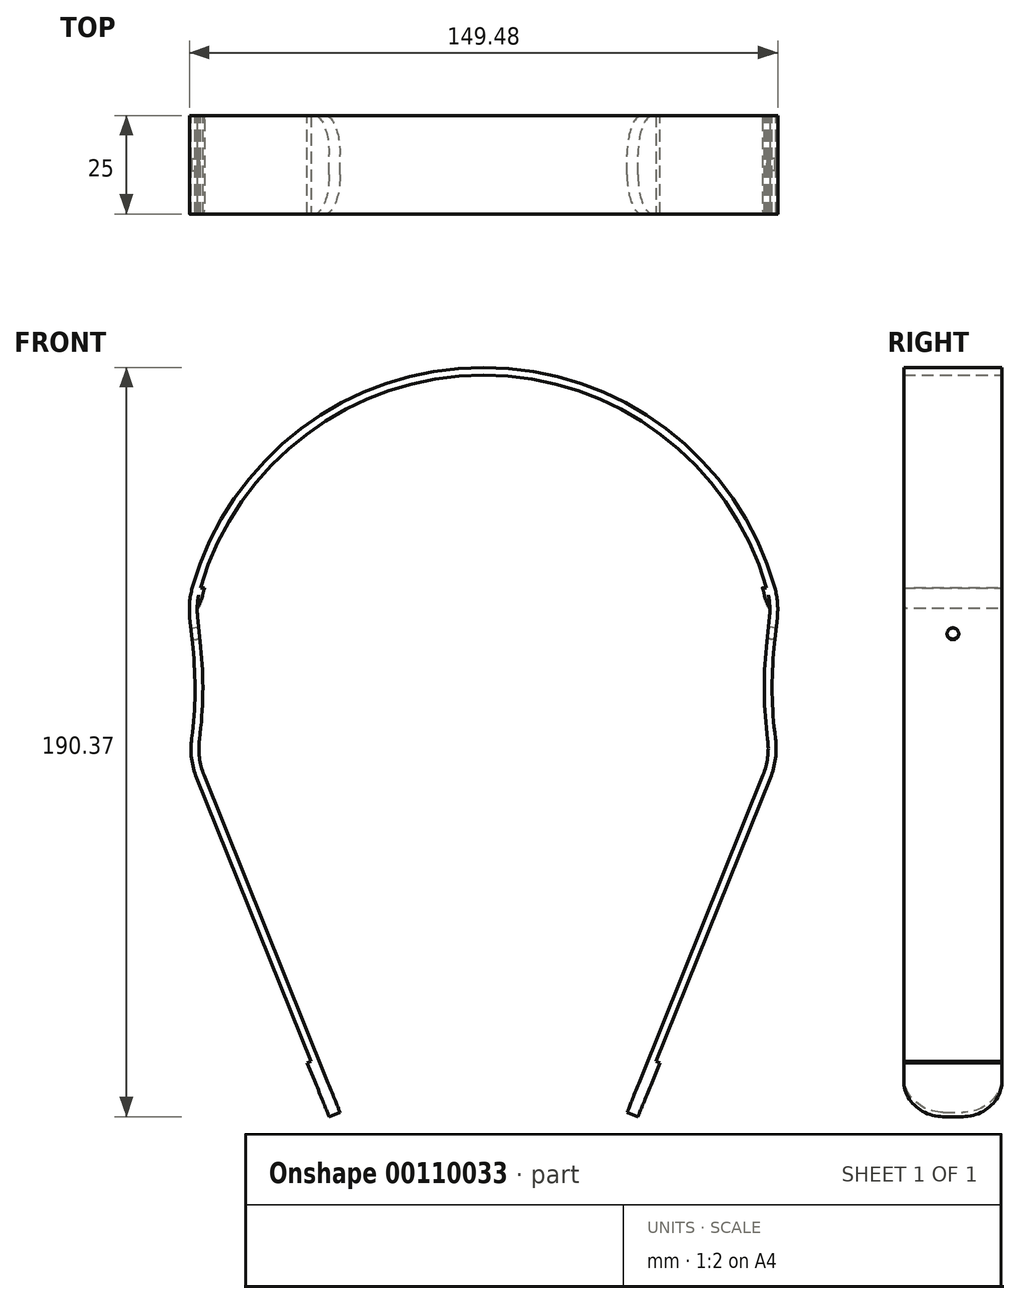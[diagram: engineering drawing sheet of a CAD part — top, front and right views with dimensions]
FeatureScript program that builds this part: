
annotation { "Feature Type Name" : "Feature", "Feature Type Description" : "" }
export const myFeature = defineFeature(function(context is Context, id is Id, definition is map)
    precondition{}
    {
        {
            var Q0;
            Q0=qCreatedBy(makeId("Front.planeOp"),FACE);
            var sketch = newSketch(context, id + "F0", { "sketchPlane" : qUnion([Q0])});
            skLineSegment(sketch, "E0", {"start": v(0, 0) * mm, "end": v(0, 60) * mm, "construction": true});
            skLineSegment(sketch, "E1", {"start": v(0, 0) * mm, "end": v(-75, 0) * mm, "construction": true});
            skArc(sketch, "E2", {"start": v(0, 60) * mm, "mid": v(-46.4, 44.41) * mm, "end": v(-74, 3.98) * mm});
            skLineSegment(sketch, "E3", {"start": v(-74.64, -3.51) * mm, "end": v(-73.83, -11.25) * mm});
            skPoint(sketch, "E4.visualSharp", {"position": v(-75, 0) * mm});
            skArc(sketch, "E4.filletArc", {"start": v(-74, 3.98) * mm, "mid": v(-74.67, 0.26) * mm, "end": v(-74.64, -3.51) * mm});
            skPoint(sketch, "E5.visualSharp", {"position": v(-73.28, -16.58) * mm});
            skArc(sketch, "E5.filletArc", {"start": v(-74.15, -34.24) * mm, "mid": v(-73.32, -22.75) * mm, "end": v(-73.83, -11.25) * mm});
            skPoint(sketch, "E6.visualSharp", {"position": v(-83.24, -38.88) * mm});
            skPoint(sketch, "E7.orphan", {"position": v(75, 0) * mm});
            skLineSegment(sketch, "E8", {"start": v(-38.32, -130) * mm, "end": v(-72.87, -44.34) * mm});
            skPoint(sketch, "E9.visualSharp", {"position": v(-74.94, -39.21) * mm});
            skArc(sketch, "E9.filletArc", {"start": v(-74.15, -34.24) * mm, "mid": v(-74.17, -39.37) * mm, "end": v(-72.87, -44.34) * mm});
            skLineSegment(sketch, "E10.0", {"start": v(-36.47, -129.25) * mm, "end": v(-71.02, -43.6) * mm});
            skArc(sketch, "E10.1", {"start": v(-72.17, -34.5) * mm, "mid": v(-72.18, -39.12) * mm, "end": v(-71.02, -43.6) * mm});
            skArc(sketch, "E10.2", {"start": v(0, 58) * mm, "mid": v(-45.2, 42.82) * mm, "end": v(-72.07, 3.44) * mm});
            skArc(sketch, "E10.3", {"start": v(-72.07, 3.44) * mm, "mid": v(-72.68, 0.1) * mm, "end": v(-72.65, -3.3) * mm});
            skLineSegment(sketch, "E10.4", {"start": v(-72.65, -3.3) * mm, "end": v(-71.84, -11.04) * mm});
            skArc(sketch, "E10.5", {"start": v(-72.17, -34.5) * mm, "mid": v(-71.32, -22.78) * mm, "end": v(-71.84, -11.04) * mm});
            skLineSegment(sketch, "E11", {"start": v(0, 58) * mm, "end": v(0, 60) * mm});
            skLineSegment(sketch, "E12", {"start": v(-38.32, -130) * mm, "end": v(-36.47, -129.25) * mm});
            skSolve(sketch);
        }
        {
            var Q0;
            Q0=makeQuery(id+"F0.imprint","IMPRINT",FACE,{"disambiguationData":[TD([[makeQuery(id+"F0.imprint","IMPRINT",EDGE,{"derivedFrom":sQuery(id+"F0.wireOp",EDGE,"E2")}),1.0]])]});
            extrude(context, id + "F1", {"entities" : qUnion([Q0]), "depth" : 25 * mm});
        }
        {
            var Q0;
            Q0=makeQuery(id+"F1.opExtrude","CAP_EDGE",EDGE,{"disambiguationData":[OSD([sQuery(id+"F0.wireOp",EDGE,"E12")])],"isStart":false});
            var Q1;
            Q1=makeQuery(id+"F1.opExtrude","CAP_EDGE",EDGE,{"disambiguationData":[OSD([sQuery(id+"F0.wireOp",EDGE,"E12")])],"isStart":true});
            fillet(context, id + "F2", {"entities" : qUnion([Q0, Q1]), "radius" : 10 * mm, "tangentPropagation" : true, "allowEdgeOverflow" : false});
        }
        {
            var Q0;
            Q0=makeQuery(id+"F1.opExtrude","SWEPT_FACE",FACE,{"disambiguationData":[OSD([sQuery(id+"F0.wireOp",EDGE,"E10.4")])]});
            var sketch = newSketch(context, id + "F3", { "sketchPlane" : qUnion([Q0])});
            skCircle(sketch, "E13", {"center": v(-12.5, 0) * mm, "radius": 1.5 * mm});
            skSolve(sketch);
        }
        {
            var Q0;
            Q0=makeQuery(id+"F3.imprint","IMPRINT",FACE,{"disambiguationData":[TD([[makeQuery(id+"F3.imprint","IMPRINT",EDGE,{"derivedFrom":sQuery(id+"F3.wireOp",EDGE,"E13")}),1.0]])]});
            extrude(context, id + "F4", {"entities" : qUnion([Q0]), "operationType" : NewBodyOperationType.REMOVE, "oppositeDirection" : true, "depth" : 25 * mm});
        }
        {
            var Q0;
            Q0=makeQuery(id+"F1.opExtrude","SWEPT_FACE",FACE,{"disambiguationData":[OSD([sQuery(id+"F0.wireOp",EDGE,"E10.0")])]});
            var sketch = newSketch(context, id + "F5", { "sketchPlane" : qUnion([Q0])});
            skLineSegment(sketch, "E14", {"start": v(-25, -91.47) * mm, "end": v(0, -91.47) * mm});
            skLineSegment(sketch, "E15.0", {"start": v(-15, -106.23) * mm, "end": v(-10, -106.23) * mm});
            skArc(sketch, "E15.1", {"start": v(-10, -106.23) * mm, "mid": v(-2.93, -103.3) * mm, "end": v(0, -96.23) * mm});
            skArc(sketch, "E15.2", {"start": v(-25, -96.23) * mm, "mid": v(-22.07, -103.3) * mm, "end": v(-15, -106.23) * mm});
            skLineSegment(sketch, "E15.3", {"start": v(-25, -96.23) * mm, "end": v(-25, -91.47) * mm});
            skLineSegment(sketch, "E15.4", {"start": v(0, -96.23) * mm, "end": v(0, -91.47) * mm});
            skSolve(sketch);
        }
        {
            var Q0;
            Q0 = qSketchRegion(id + "F5", true);
            extrude(context, id + "F6", {"entities" : qUnion([Q0]), "operationType" : NewBodyOperationType.ADD, "oppositeDirection" : true, "depth" : 3 * mm});
        }
        {
            var Q0;
            Q0=makeQuery(id+"F1.opExtrude","CAP_FACE",FACE,{"disambiguationData":[OSD([sQuery(id+"F0.wireOp",EDGE,"E2"),sQuery(id+"F0.wireOp",EDGE,"E3"),sQuery(id+"F0.wireOp",EDGE,"1wV9M4SY-0Tcg-7qVq-NvGt-HIeoEMau5aPd"),sQuery(id+"F0.wireOp",EDGE,"iLl2rIAe-G8ji-OYbe-38eC-7W4aVokNutVx"),sQuery(id+"F0.wireOp",EDGE,"E4.filletArc"),sQuery(id+"F0.wireOp",EDGE,"E5.filletArc"),sQuery(id+"F0.wireOp",EDGE,"E6.filletArc"),sQuery(id+"F0.wireOp",EDGE,"2d613b12-5e41-47b2-b1e7-1da42f7e35f0.0"),sQuery(id+"F0.wireOp",EDGE,"2d613b12-5e41-47b2-b1e7-1da42f7e35f0.1"),sQuery(id+"F0.wireOp",EDGE,"2d613b12-5e41-47b2-b1e7-1da42f7e35f0.2"),sQuery(id+"F0.wireOp",EDGE,"2d613b12-5e41-47b2-b1e7-1da42f7e35f0.3"),sQuery(id+"F0.wireOp",EDGE,"2d613b12-5e41-47b2-b1e7-1da42f7e35f0.4"),sQuery(id+"F0.wireOp",EDGE,"2d613b12-5e41-47b2-b1e7-1da42f7e35f0.5"),sQuery(id+"F0.wireOp",EDGE,"2d613b12-5e41-47b2-b1e7-1da42f7e35f0.6"),sQuery(id+"F0.wireOp",EDGE,"S7WwmdWu-URVW-F1e6-4neb-kDyBiWFopnJt"),sQuery(id+"F0.wireOp",EDGE,"ds6R0Cvm-0czy-QIpx-gWQ6-nUP3UNufb8Tw")])],"isStart":false});
            var sketch = newSketch(context, id + "F7", { "sketchPlane" : qUnion([Q0])});
            skLineSegment(sketch, "E16", {"start": v(-74, 3.98) * mm, "end": v(-70.85, 3.98) * mm});
            skArc(sketch, "E17.0", {"start": v(-70.85, 3.98) * mm, "mid": v(-71.64, 0.43) * mm, "end": v(-71.65, -3.2) * mm});
            skLineSegment(sketch, "E18", {"start": v(-74.64, -3.51) * mm, "end": v(-71.65, -3.2) * mm});
            skArc(sketch, "E19.0", {"start": v(-74, 3.98) * mm, "mid": v(-74.67, 0.26) * mm, "end": v(-74.64, -3.51) * mm});
            skSolve(sketch);
        }
        {
            var Q0;
            Q0=makeQuery(id+"F7.imprint","IMPRINT",FACE,{"disambiguationData":[TD([[makeQuery(id+"F7.imprint","IMPRINT",EDGE,{"derivedFrom":sQuery(id+"F7.wireOp",EDGE,"E16")}),-1.0]])]});
            extrude(context, id + "F8", {"entities" : qUnion([Q0]), "oppositeDirection" : true, "depth" : 25 * mm});
        }
        {
            var Q0;
            Q0=makeQuery(id+"F8.opExtrude","SWEPT_EDGE",EDGE,{"disambiguationData":[OSD([sQuery(id+"F7.wireOp",EDGE,"E17.0"),sQuery(id+"F7.wireOp",EDGE,"E18")])]});
            fillet(context, id + "F9", {"entities" : qUnion([Q0]), "radius" : 10 * mm, "tangentPropagation" : true, "allowEdgeOverflow" : false});
        }
        {
            var Q0;
            Q0=makeQuery(id+"F1.opExtrude","SWEPT_BODY",BODY,{"disambiguationData":[OSD([sQuery(id+"F0.wireOp",EDGE,"E2"),sQuery(id+"F0.wireOp",EDGE,"E3"),sQuery(id+"F0.wireOp",EDGE,"1wV9M4SY-0Tcg-7qVq-NvGt-HIeoEMau5aPd"),sQuery(id+"F0.wireOp",EDGE,"iLl2rIAe-G8ji-OYbe-38eC-7W4aVokNutVx"),sQuery(id+"F0.wireOp",EDGE,"E4.filletArc"),sQuery(id+"F0.wireOp",EDGE,"E5.filletArc"),sQuery(id+"F0.wireOp",EDGE,"E6.filletArc"),sQuery(id+"F0.wireOp",EDGE,"2d613b12-5e41-47b2-b1e7-1da42f7e35f0.0"),sQuery(id+"F0.wireOp",EDGE,"2d613b12-5e41-47b2-b1e7-1da42f7e35f0.1"),sQuery(id+"F0.wireOp",EDGE,"2d613b12-5e41-47b2-b1e7-1da42f7e35f0.2"),sQuery(id+"F0.wireOp",EDGE,"2d613b12-5e41-47b2-b1e7-1da42f7e35f0.3"),sQuery(id+"F0.wireOp",EDGE,"2d613b12-5e41-47b2-b1e7-1da42f7e35f0.4"),sQuery(id+"F0.wireOp",EDGE,"2d613b12-5e41-47b2-b1e7-1da42f7e35f0.5"),sQuery(id+"F0.wireOp",EDGE,"2d613b12-5e41-47b2-b1e7-1da42f7e35f0.6"),sQuery(id+"F0.wireOp",EDGE,"S7WwmdWu-URVW-F1e6-4neb-kDyBiWFopnJt"),sQuery(id+"F0.wireOp",EDGE,"ds6R0Cvm-0czy-QIpx-gWQ6-nUP3UNufb8Tw")])]});
            var Q1;
            Q1=makeQuery(id+"F8.opExtrude","SWEPT_BODY",BODY,{"disambiguationData":[OSD([sQuery(id+"F7.wireOp",EDGE,"E16"),sQuery(id+"F7.wireOp",EDGE,"E17.0"),sQuery(id+"F7.wireOp",EDGE,"E18"),sQuery(id+"F7.wireOp",EDGE,"E19.0")])]});
            booleanBodies(context, id + "F10", {"operationType" : BooleanOperationType.UNION, "tools" : qUnion([Q0, Q1])});
        }
        {
            var Q0;
            Q0=qCreatedBy(makeId("Right.planeOp"),FACE);
            var sketch = newSketch(context, id + "F11", { "sketchPlane" : qUnion([Q0])});
            skCircle(sketch, "E20", {"center": v(12.5, 8.98) * mm, "radius": 1.5 * mm});
            skSolve(sketch);
        }
        {
            var Q0;
            Q0=makeQuery(id+"F11.imprint","IMPRINT",FACE,{"disambiguationData":[TD([[makeQuery(id+"F11.imprint","IMPRINT",EDGE,{"derivedFrom":sQuery(id+"F11.wireOp",EDGE,"E20")}),1.0]])]});
            extrude(context, id + "F12", {"entities" : qUnion([Q0]), "operationType" : NewBodyOperationType.REMOVE, "oppositeDirection" : true, "depth" : 111.65 * mm});
        }
        {
            var Q0;
            Q0=makeQuery(id+"F1.opExtrude","SWEPT_BODY",BODY,{"disambiguationData":[OSD([sQuery(id+"F0.wireOp",EDGE,"E2"),sQuery(id+"F0.wireOp",EDGE,"E3"),sQuery(id+"F0.wireOp",EDGE,"1wV9M4SY-0Tcg-7qVq-NvGt-HIeoEMau5aPd"),sQuery(id+"F0.wireOp",EDGE,"iLl2rIAe-G8ji-OYbe-38eC-7W4aVokNutVx"),sQuery(id+"F0.wireOp",EDGE,"E4.filletArc"),sQuery(id+"F0.wireOp",EDGE,"E5.filletArc"),sQuery(id+"F0.wireOp",EDGE,"E6.filletArc"),sQuery(id+"F0.wireOp",EDGE,"2d613b12-5e41-47b2-b1e7-1da42f7e35f0.0"),sQuery(id+"F0.wireOp",EDGE,"2d613b12-5e41-47b2-b1e7-1da42f7e35f0.1"),sQuery(id+"F0.wireOp",EDGE,"2d613b12-5e41-47b2-b1e7-1da42f7e35f0.2"),sQuery(id+"F0.wireOp",EDGE,"2d613b12-5e41-47b2-b1e7-1da42f7e35f0.3"),sQuery(id+"F0.wireOp",EDGE,"2d613b12-5e41-47b2-b1e7-1da42f7e35f0.4"),sQuery(id+"F0.wireOp",EDGE,"2d613b12-5e41-47b2-b1e7-1da42f7e35f0.5"),sQuery(id+"F0.wireOp",EDGE,"2d613b12-5e41-47b2-b1e7-1da42f7e35f0.6"),sQuery(id+"F0.wireOp",EDGE,"S7WwmdWu-URVW-F1e6-4neb-kDyBiWFopnJt"),sQuery(id+"F0.wireOp",EDGE,"ds6R0Cvm-0czy-QIpx-gWQ6-nUP3UNufb8Tw")])]});
            var Q1;
            Q1=qCreatedBy(makeId("Right.planeOp"),FACE);
            mirror(context, id + "F13", {"operationType" : NewBodyOperationType.ADD, "entities" : qUnion([Q0]), "mirrorPlane" : qUnion([Q1])});
        }
        {
            var Q0;
            {var subQ0=sQuery(id+"F7.wireOp",EDGE,"E18");var subQ1=sQuery(id+"F7.wireOp",EDGE,"E17.0");Q0=makeQuery(id+"F13.opPattern","COPY",EDGE,{"derivedFrom":makeQuery(id+"F9.opFillet","BLEND_EDGE",EDGE,{"blendedFrom":[makeQuery(id+"F8.opExtrude","SWEPT_EDGE",EDGE,{"disambiguationData":[OSD([subQ1,subQ0])]}),makeQuery(id+"F8.opExtrude","CAP_FACE",FACE,{"disambiguationData":[OSD([sQuery(id+"F7.wireOp",EDGE,"E16"),subQ1,subQ0,sQuery(id+"F7.wireOp",EDGE,"E19.0")])],"isStart":false})],"blendedInto":[makeQuery(id+"F8.opExtrude","CAP_FACE",FACE,{"disambiguationData":[OSD([sQuery(id+"F7.wireOp",EDGE,"E16"),subQ1,subQ0,sQuery(id+"F7.wireOp",EDGE,"E19.0")])],"isStart":false})]}),"instanceName":"1"});}
            var Q1;
            {var subQ0=sQuery(id+"F7.wireOp",EDGE,"E18");var subQ1=sQuery(id+"F7.wireOp",EDGE,"E17.0");Q1=makeQuery(id+"F13.opPattern","COPY",EDGE,{"derivedFrom":makeQuery(id+"F9.opFillet","BLEND_EDGE",EDGE,{"blendedFrom":[makeQuery(id+"F8.opExtrude","SWEPT_EDGE",EDGE,{"disambiguationData":[OSD([subQ1,subQ0])]}),makeQuery(id+"F8.opExtrude","CAP_FACE",FACE,{"disambiguationData":[OSD([sQuery(id+"F7.wireOp",EDGE,"E16"),subQ1,subQ0,sQuery(id+"F7.wireOp",EDGE,"E19.0")])],"isStart":true})],"blendedInto":[makeQuery(id+"F8.opExtrude","CAP_FACE",FACE,{"disambiguationData":[OSD([sQuery(id+"F7.wireOp",EDGE,"E16"),subQ1,subQ0,sQuery(id+"F7.wireOp",EDGE,"E19.0")])],"isStart":true})]}),"instanceName":"1"});}
            var Q2;
            {var subQ0=sQuery(id+"F7.wireOp",EDGE,"E18");var subQ1=sQuery(id+"F7.wireOp",EDGE,"E17.0");Q2=makeQuery(id+"F9.opFillet","BLEND_EDGE",EDGE,{"blendedFrom":[makeQuery(id+"F8.opExtrude","SWEPT_EDGE",EDGE,{"disambiguationData":[OSD([subQ1,subQ0])]}),makeQuery(id+"F8.opExtrude","CAP_FACE",FACE,{"disambiguationData":[OSD([sQuery(id+"F7.wireOp",EDGE,"E16"),subQ1,subQ0,sQuery(id+"F7.wireOp",EDGE,"E19.0")])],"isStart":false})],"blendedInto":[makeQuery(id+"F8.opExtrude","CAP_FACE",FACE,{"disambiguationData":[OSD([sQuery(id+"F7.wireOp",EDGE,"E16"),subQ1,subQ0,sQuery(id+"F7.wireOp",EDGE,"E19.0")])],"isStart":false})]});}
            var Q3;
            {var subQ0=sQuery(id+"F7.wireOp",EDGE,"E18");var subQ1=sQuery(id+"F7.wireOp",EDGE,"E17.0");Q3=makeQuery(id+"F9.opFillet","BLEND_EDGE",EDGE,{"blendedFrom":[makeQuery(id+"F8.opExtrude","SWEPT_EDGE",EDGE,{"disambiguationData":[OSD([subQ1,subQ0])]}),makeQuery(id+"F8.opExtrude","CAP_FACE",FACE,{"disambiguationData":[OSD([sQuery(id+"F7.wireOp",EDGE,"E16"),subQ1,subQ0,sQuery(id+"F7.wireOp",EDGE,"E19.0")])],"isStart":true})],"blendedInto":[makeQuery(id+"F8.opExtrude","CAP_FACE",FACE,{"disambiguationData":[OSD([sQuery(id+"F7.wireOp",EDGE,"E16"),subQ1,subQ0,sQuery(id+"F7.wireOp",EDGE,"E19.0")])],"isStart":true})]});}
            fillet(context, id + "F14", {"entities" : qUnion([Q0, Q1, Q2, Q3]), "radius" : 1 * mm, "tangentPropagation" : true, "allowEdgeOverflow" : false});
        }
    });
